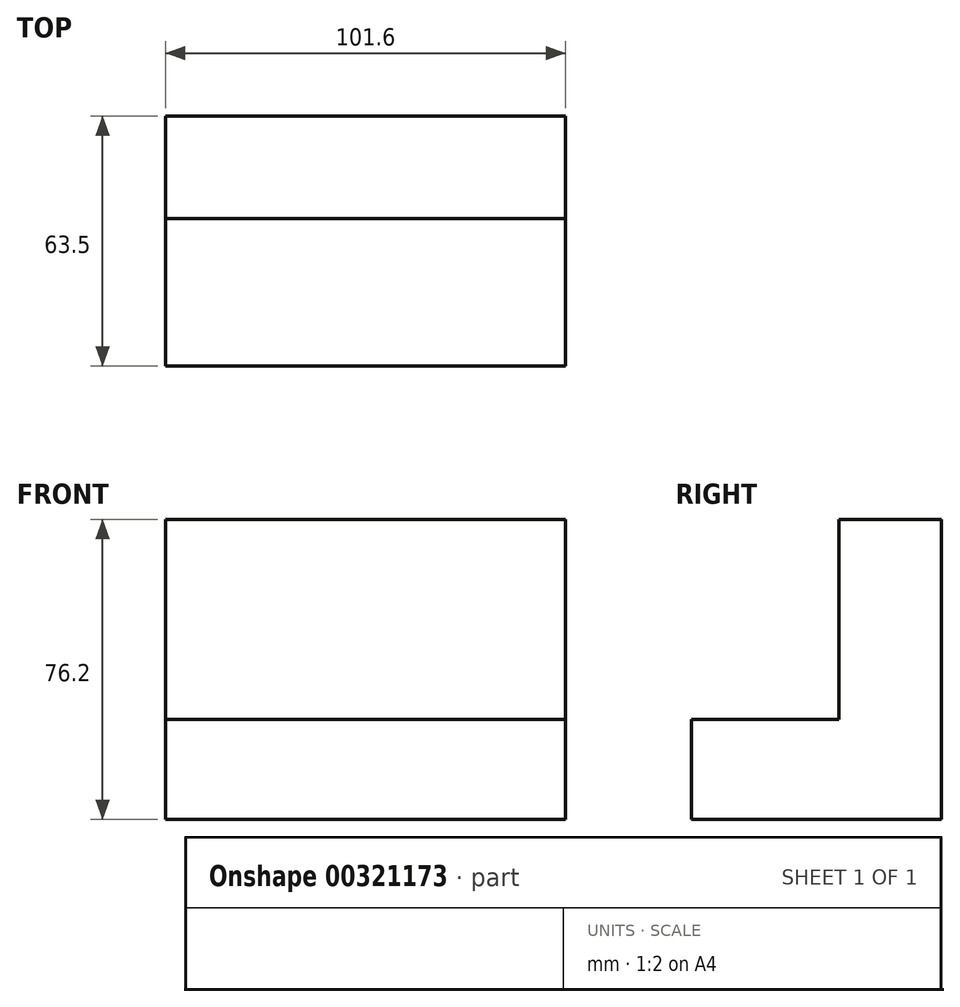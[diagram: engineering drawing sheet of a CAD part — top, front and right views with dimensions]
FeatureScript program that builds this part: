
annotation { "Feature Type Name" : "Feature", "Feature Type Description" : "" }
export const myFeature = defineFeature(function(context is Context, id is Id, definition is map)
    precondition{}
    {
        {
            var Q0;
            Q0=qCreatedBy(makeId("Right.planeOp"),FACE);
            var sketch = newSketch(context, id + "F0", { "sketchPlane" : qUnion([Q0])});
            skLineSegment(sketch, "E0", {"start": v(-32.37, -43.22) * mm, "end": v(31.13, -43.22) * mm});
            skLineSegment(sketch, "E1", {"start": v(31.13, -43.22) * mm, "end": v(31.13, 32.98) * mm});
            skLineSegment(sketch, "E2", {"start": v(31.13, 32.98) * mm, "end": v(5.13, 32.98) * mm});
            skLineSegment(sketch, "E3", {"start": v(5.13, 32.98) * mm, "end": v(5.13, -17.82) * mm});
            skLineSegment(sketch, "E4", {"start": v(5.13, -17.82) * mm, "end": v(-32.37, -17.82) * mm});
            skLineSegment(sketch, "E5", {"start": v(-32.37, -17.82) * mm, "end": v(-32.37, -43.22) * mm});
            skSolve(sketch);
        }
        {
            var Q0;
            Q0=makeQuery(id+"F0.imprint","IMPRINT",FACE,{"disambiguationData":[TD([[makeQuery(id+"F0.imprint","IMPRINT",EDGE,{"derivedFrom":sQuery(id+"F0.wireOp",EDGE,"E0")}),1.0]])]});
            extrude(context, id + "F1", {"entities" : qUnion([Q0]), "oppositeDirection" : true, "depth" : 101.6 * mm});
        }
        {
            var Q0;
            Q0=makeQuery(id+"F1.opExtrude","SWEPT_FACE",FACE,{"disambiguationData":[OSD([sQuery(id+"F0.wireOp",EDGE,"E3")])]});
            var sketch = newSketch(context, id + "F2", { "sketchPlane" : qUnion([Q0])});
            skLineSegment(sketch, "E6", {"start": v(-76.47, 32.98) * mm, "end": v(-76.47, 0) * mm});
            skLineSegment(sketch, "E7", {"start": v(-76.47, 0) * mm, "end": v(-25.67, 0) * mm});
            skLineSegment(sketch, "E8", {"start": v(-25.67, 0) * mm, "end": v(-25.67, 32.98) * mm});
            skSolve(sketch);
        }
        {
            var Q0;
            {var subQ0=sQuery(id+"F2.wireOp",EDGE,"E6");Q0=makeQuery(id+"F2.imprint","IMPRINT",FACE,{"disambiguationData":[TD([[makeQuery(id+"F2.imprint","IMPRINT",EDGE,{"derivedFrom":subQ0}),1.0]])]});}
            extrude(context, id + "F3", {"entities" : qUnion([Q0]), "operationType" : NewBodyOperationType.ADD, "oppositeDirection" : true, "depth" : 25.4 * mm});
        }
    });
